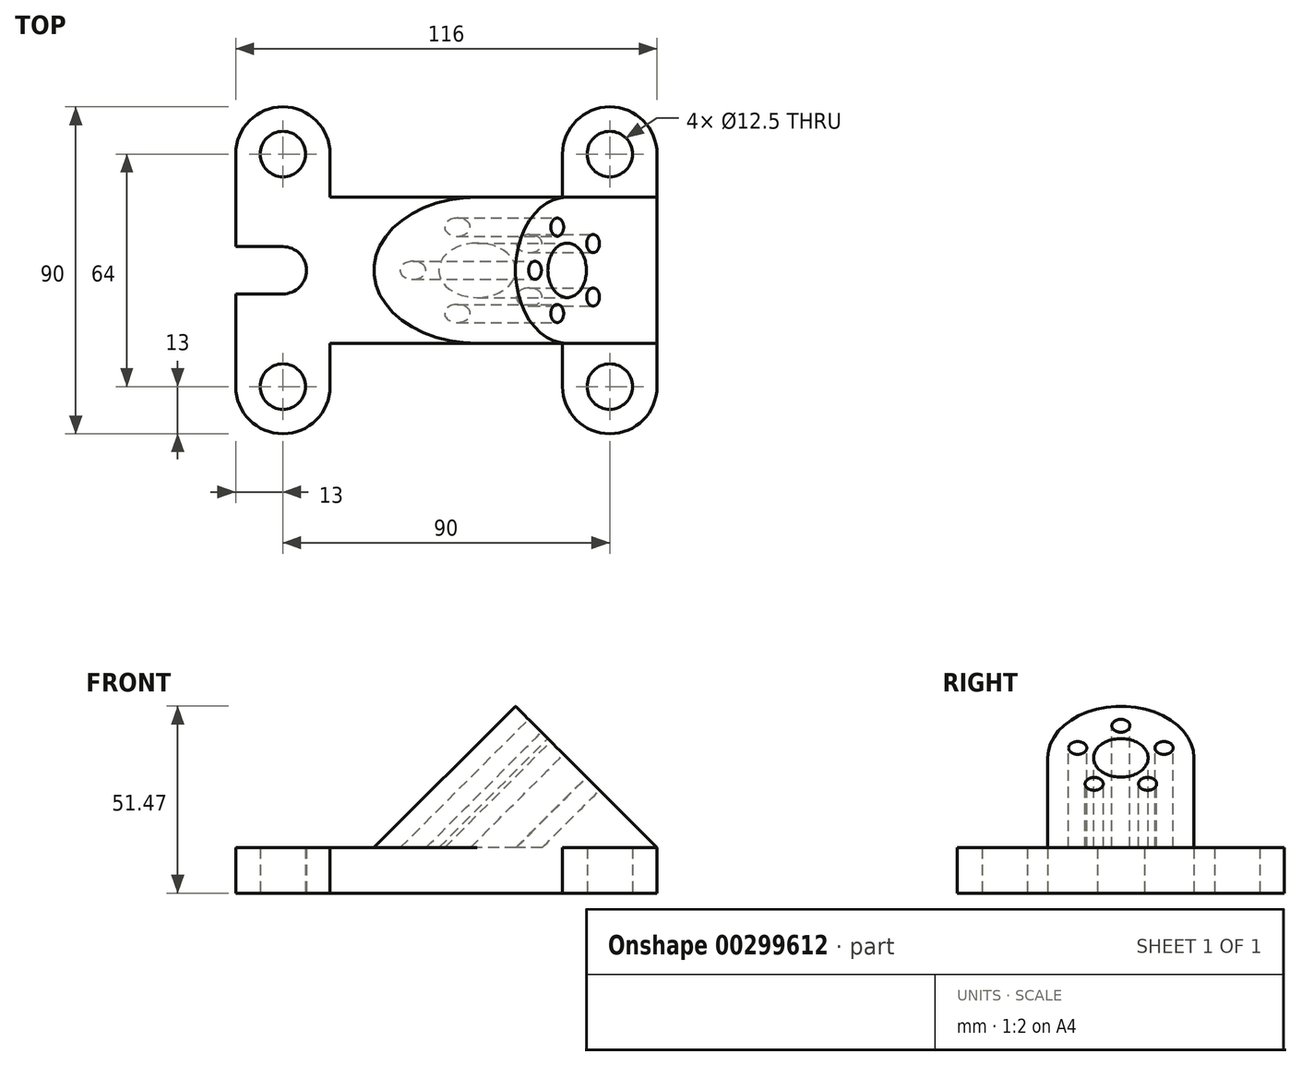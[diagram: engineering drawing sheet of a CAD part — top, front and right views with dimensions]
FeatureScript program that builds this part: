
annotation { "Feature Type Name" : "Feature", "Feature Type Description" : "" }
export const myFeature = defineFeature(function(context is Context, id is Id, definition is map)
    precondition{}
    {
        {
            var Q0;
            Q0=qCreatedBy(makeId("Top.planeOp"),FACE);
            var sketch = newSketch(context, id + "F0", { "sketchPlane" : qUnion([Q0])});
            skLineSegment(sketch, "E0", {"start": v(0, 6.5) * mm, "end": v(0, 32) * mm});
            skLineSegment(sketch, "E1", {"start": v(26, 32) * mm, "end": v(26, 20.1) * mm});
            skLineSegment(sketch, "E2", {"start": v(26, 20.1) * mm, "end": v(90, 20.1) * mm});
            skLineSegment(sketch, "E3", {"start": v(90, 20.1) * mm, "end": v(90, 32) * mm});
            skLineSegment(sketch, "E4", {"start": v(116, 32) * mm, "end": v(116, -32) * mm});
            skLineSegment(sketch, "E5", {"start": v(90, -32) * mm, "end": v(90, -20.1) * mm});
            skLineSegment(sketch, "E6", {"start": v(90, -20.1) * mm, "end": v(26, -20.1) * mm});
            skLineSegment(sketch, "E7", {"start": v(26, -20.1) * mm, "end": v(26, -32) * mm});
            skLineSegment(sketch, "E8", {"start": v(0, -32) * mm, "end": v(0, -6.5) * mm});
            skLineSegment(sketch, "E9", {"start": v(0, -6.5) * mm, "end": v(13, -6.5) * mm});
            skLineSegment(sketch, "E10", {"start": v(13, 6.5) * mm, "end": v(0, 6.5) * mm});
            skArc(sketch, "E11", {"start": v(26, 32) * mm, "mid": v(13, 45) * mm, "end": v(0, 32) * mm});
            skArc(sketch, "E12", {"start": v(116, 32) * mm, "mid": v(103, 45) * mm, "end": v(90, 32) * mm});
            skArc(sketch, "E13", {"start": v(0, -32) * mm, "mid": v(13, -45) * mm, "end": v(26, -32) * mm});
            skArc(sketch, "E14", {"start": v(90, -32) * mm, "mid": v(103, -45) * mm, "end": v(116, -32) * mm});
            skCircle(sketch, "E15", {"center": v(13, 32) * mm, "radius": 6.25 * mm});
            skCircle(sketch, "E16", {"center": v(103, 32) * mm, "radius": 6.25 * mm});
            skCircle(sketch, "E17", {"center": v(13, -32) * mm, "radius": 6.25 * mm});
            skCircle(sketch, "E18", {"center": v(103, -32) * mm, "radius": 6.25 * mm});
            skArc(sketch, "E19", {"start": v(13, -6.5) * mm, "mid": v(19.5, 0) * mm, "end": v(13, 6.5) * mm});
            skSolve(sketch);
        }
        {
            var Q0;
            Q0 = qSketchRegion(id + "F0", true);
            extrude(context, id + "F1", {"entities" : qUnion([Q0]), "depth" : 12.5 * mm});
        }
        {
            var Q0;
            Q0=makeQuery(id+"F1.opExtrude","CAP_EDGE",EDGE,{"disambiguationData":[OSD([sQuery(id+"F0.wireOp",EDGE,"E4")])],"isStart":false});
            var Q1;
            Q1=qCreatedBy(makeId("Right.planeOp"),FACE);
            cPlane(context, id + "F2", {"entities" : qUnion([Q0, Q1]), "cplaneType" : CPlaneType.LINE_ANGLE, "offset" : 25 * mm, "angle" : 45 * degree, "width" : 150 * mm, "height" : 150 * mm});
        }
        {
            var Q0;
            Q0=qCreatedBy(id+"F2.planeOp",FACE);
            var sketch = newSketch(context, id + "F3", { "sketchPlane" : qUnion([Q0])});
            skLineSegment(sketch, "E20", {"start": v(20.1, -73.19) * mm, "end": v(20.1, -38.19) * mm});
            skLineSegment(sketch, "E21", {"start": v(-20.1, -38.19) * mm, "end": v(-20.1, -73.19) * mm});
            skArc(sketch, "E22", {"start": v(20.1, -38.19) * mm, "mid": v(0, -18.08) * mm, "end": v(-20.1, -38.19) * mm});
            skCircle(sketch, "E23", {"center": v(0, -38.19) * mm, "radius": 7.5 * mm});
            skCircle(sketch, "E24", {"center": v(0, -25.69) * mm, "radius": 2.5 * mm});
            skPoint(sketch, "E24.centerSnap0", {"position": v(0, -18.08) * mm});
            skCircle(sketch, "E25.1.0", {"center": v(-11.89, -34.32) * mm, "radius": 2.5 * mm});
            skCircle(sketch, "E25.2.0", {"center": v(-7.35, -48.3) * mm, "radius": 2.5 * mm});
            skCircle(sketch, "E25.3.0", {"center": v(7.35, -48.3) * mm, "radius": 2.5 * mm});
            skCircle(sketch, "E25.4.0", {"center": v(11.89, -34.32) * mm, "radius": 2.5 * mm});
            skLineSegment(sketch, "E26", {"start": v(20.1, -73.19) * mm, "end": v(-20.1, -73.19) * mm});
            skSolve(sketch);
        }
        {
            var Q0;
            Q0=makeQuery(id+"F3.imprint","IMPRINT",FACE,{"disambiguationData":[TD([[makeQuery(id+"F3.imprint","IMPRINT",EDGE,{"derivedFrom":sQuery(id+"F3.wireOp",EDGE,"E20")}),1.0]])]});
            var Q1;
            Q1=makeQuery(id+"F1.opExtrude","CAP_FACE",FACE,{"disambiguationData":[OSD([sQuery(id+"F0.wireOp",EDGE,"E0"),sQuery(id+"F0.wireOp",EDGE,"E1"),sQuery(id+"F0.wireOp",EDGE,"E2"),sQuery(id+"F0.wireOp",EDGE,"E3"),sQuery(id+"F0.wireOp",EDGE,"E4"),sQuery(id+"F0.wireOp",EDGE,"E5"),sQuery(id+"F0.wireOp",EDGE,"E6"),sQuery(id+"F0.wireOp",EDGE,"E7"),sQuery(id+"F0.wireOp",EDGE,"E8"),sQuery(id+"F0.wireOp",EDGE,"E9"),sQuery(id+"F0.wireOp",EDGE,"E10"),sQuery(id+"F0.wireOp",EDGE,"E11"),sQuery(id+"F0.wireOp",EDGE,"E12"),sQuery(id+"F0.wireOp",EDGE,"E13"),sQuery(id+"F0.wireOp",EDGE,"E14"),sQuery(id+"F0.wireOp",EDGE,"E15"),sQuery(id+"F0.wireOp",EDGE,"E16"),sQuery(id+"F0.wireOp",EDGE,"E17"),sQuery(id+"F0.wireOp",EDGE,"E18"),sQuery(id+"F0.wireOp",EDGE,"E19")])],"isStart":true});
            extrude(context, id + "F4", {"entities" : qUnion([Q0]), "operationType" : NewBodyOperationType.ADD, "endBound" : BoundingType.UP_TO_SURFACE, "endBoundEntityFace" : qUnion([Q1]), "depth" : 25 * mm});
        }
    });
